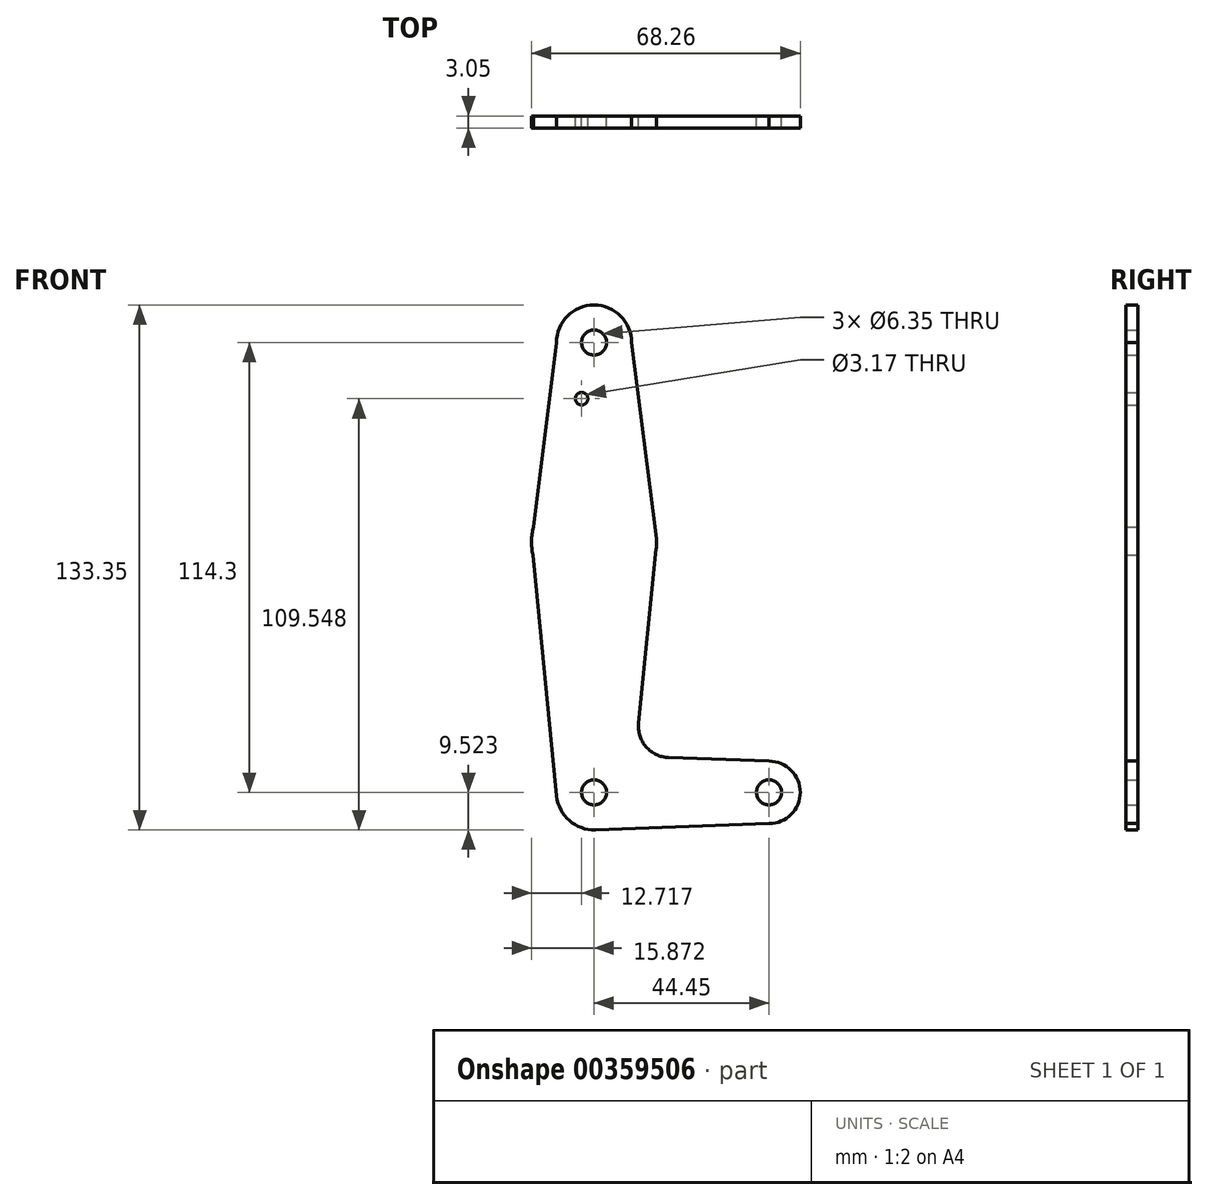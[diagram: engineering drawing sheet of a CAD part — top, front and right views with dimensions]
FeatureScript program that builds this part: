
annotation { "Feature Type Name" : "Feature", "Feature Type Description" : "" }
export const myFeature = defineFeature(function(context is Context, id is Id, definition is map)
    precondition{}
    {
        {
            var Q0;
            Q0=qCreatedBy(makeId("Front.planeOp"),FACE);
            var sketch = newSketch(context, id + "F0", { "sketchPlane" : qUnion([Q0])});
            skCircle(sketch, "E0", {"center": v(-18.97, 57.2) * mm, "radius": 9.53 * mm});
            skCircle(sketch, "E1", {"center": v(-18.97, 6.4) * mm, "radius": 15.88 * mm});
            skCircle(sketch, "E2", {"center": v(-18.97, -57.1) * mm, "radius": 9.53 * mm});
            skCircle(sketch, "E3", {"center": v(25.48, -57.1) * mm, "radius": 7.94 * mm});
            skLineSegment(sketch, "E4", {"start": v(-18.97, -57.1) * mm, "end": v(-18.97, 6.4) * mm, "construction": true});
            skLineSegment(sketch, "E5", {"start": v(-18.97, 57.2) * mm, "end": v(-18.97, -57.1) * mm, "construction": true});
            skLineSegment(sketch, "E6", {"start": v(-18.97, -57.1) * mm, "end": v(25.48, -57.1) * mm, "construction": true});
            skLineSegment(sketch, "E7", {"start": v(-28.5, 57.2) * mm, "end": v(-34.84, 6.4) * mm});
            skLineSegment(sketch, "E8", {"start": v(-9.44, 57.2) * mm, "end": v(-2.96, 6.4) * mm});
            skLineSegment(sketch, "E9", {"start": v(-28.45, -58.05) * mm, "end": v(-34.84, 6.45) * mm});
            skLineSegment(sketch, "E10", {"start": v(-7.66, -39.5) * mm, "end": v(-3.17, 4.8) * mm});
            skCircle(sketch, "E11", {"center": v(-18.97, 57.2) * mm, "radius": 3.18 * mm});
            skCircle(sketch, "E12", {"center": v(-22.12, 42.92) * mm, "radius": 1.59 * mm});
            skLineSegment(sketch, "E13", {"start": v(25.48, -49.17) * mm, "end": v(-0.04, -48.25) * mm});
            skLineSegment(sketch, "E14", {"start": v(25.48, -65.04) * mm, "end": v(-18.63, -66.63) * mm});
            skCircle(sketch, "E15", {"center": v(-18.97, -57.1) * mm, "radius": 3.18 * mm});
            skArc(sketch, "E16.filletArc", {"start": v(-7.66, -39.5) * mm, "mid": v(-5.74, -45.53) * mm, "end": v(-0.04, -48.25) * mm});
            skCircle(sketch, "E17", {"center": v(25.48, -57.1) * mm, "radius": 3.18 * mm});
            skSolve(sketch);
        }
        {
            var Q0;
            Q0 = qSketchRegion(id + "F0", true);
            extrude(context, id + "F1", {"entities" : qUnion([Q0]), "depth" : 3.05 * mm});
        }
    });
